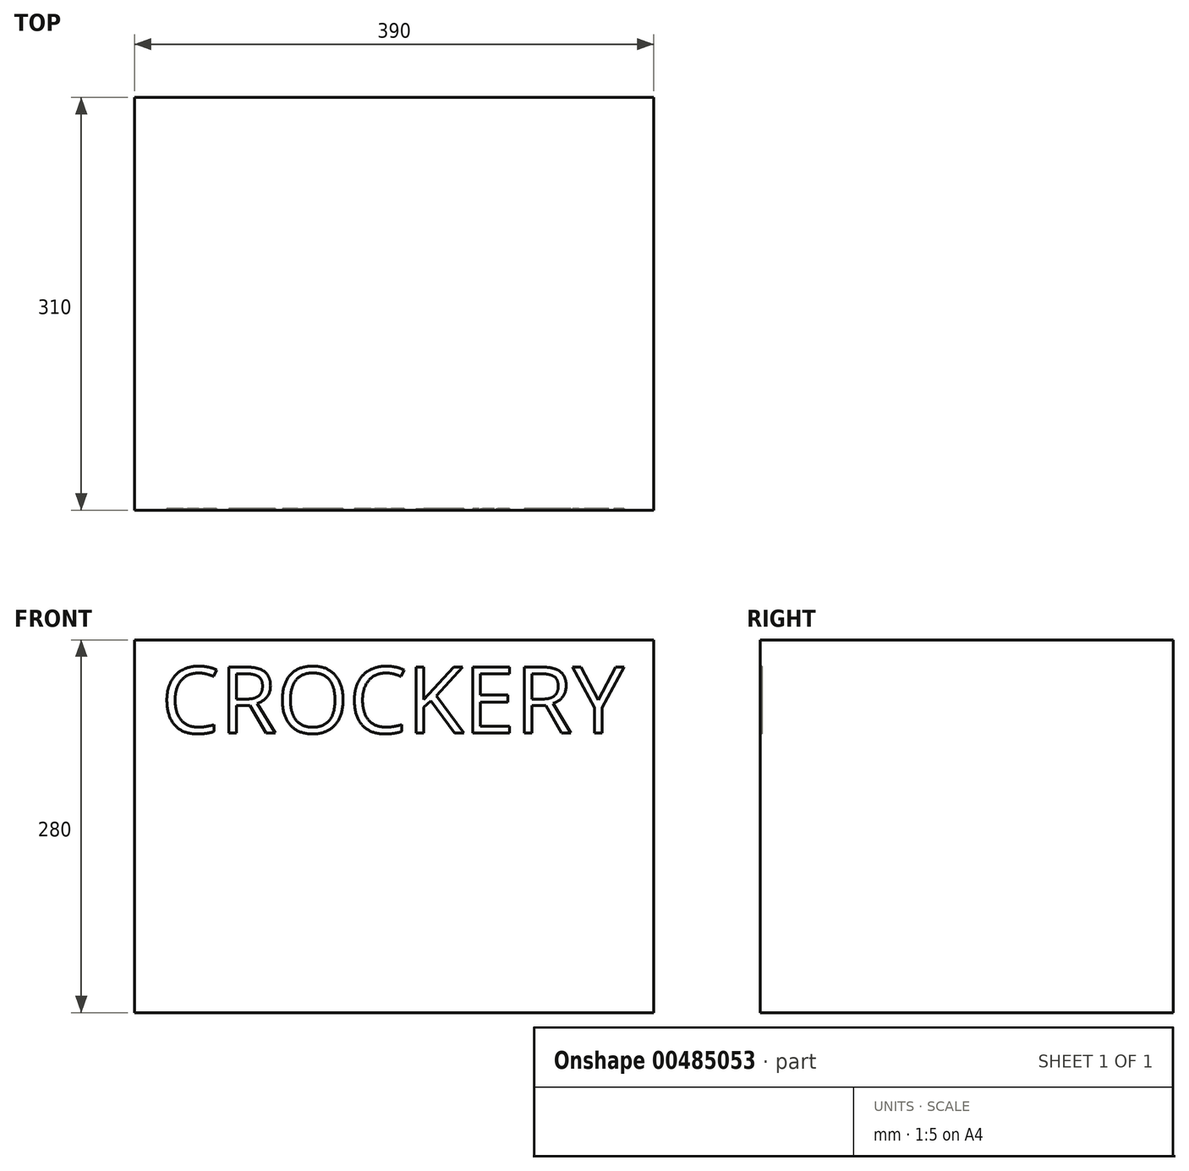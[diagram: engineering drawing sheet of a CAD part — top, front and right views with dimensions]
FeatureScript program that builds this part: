
annotation { "Feature Type Name" : "Feature", "Feature Type Description" : "" }
export const myFeature = defineFeature(function(context is Context, id is Id, definition is map)
    precondition{}
    {
        {
            var Q0;
            Q0=qCreatedBy(makeId("Top.planeOp"),FACE);
            var sketch = newSketch(context, id + "F0", { "sketchPlane" : qUnion([Q0])});
            skLineSegment(sketch, "E0.bottom", {"start": v(195, -155) * mm, "end": v(-195, -155) * mm});
            skLineSegment(sketch, "E0.top", {"start": v(195, 155) * mm, "end": v(-195, 155) * mm});
            skLineSegment(sketch, "E0.left", {"start": v(195, -155) * mm, "end": v(195, 155) * mm});
            skLineSegment(sketch, "E0.right", {"start": v(-195, -155) * mm, "end": v(-195, 155) * mm});
            skPoint(sketch, "E0.middle", {"position": v(0, 0) * mm});
            skSolve(sketch);
        }
        {
            var Q0;
            Q0=makeQuery(id+"F0.imprint","IMPRINT",FACE,{"disambiguationData":[TD([[makeQuery(id+"F0.imprint","IMPRINT",EDGE,{"derivedFrom":sQuery(id+"F0.wireOp",EDGE,"E0.bottom")}),-1.0]])]});
            extrude(context, id + "F1", {"entities" : qUnion([Q0]), "depth" : 280 * mm});
        }
        {
            var Q0;
            Q0=makeQuery(id+"F1.opExtrude","SWEPT_FACE",FACE,{"disambiguationData":[OSD([sQuery(id+"F0.wireOp",EDGE,"E0.bottom")])]});
            var sketch = newSketch(context, id + "F2", { "sketchPlane" : qUnion([Q0])});
            skText(sketch, "E1", { "text": "CROCKERY", "fontName": "OpenSans-Regular.ttf"});
            const initialGuessF2  = {"E1": [-0.175, 0.21, 1, 0, 0.05]};
            skSetInitialGuess(sketch, initialGuessF2);
            skSolve(sketch);
        }
        {
            var Q0;
            Q0 = qSketchRegion(id + "F2", true);
            extrude(context, id + "F3", {"entities" : qUnion([Q0]), "operationType" : NewBodyOperationType.REMOVE, "oppositeDirection" : true, "depth" : 1 * mm});
        }
    });
